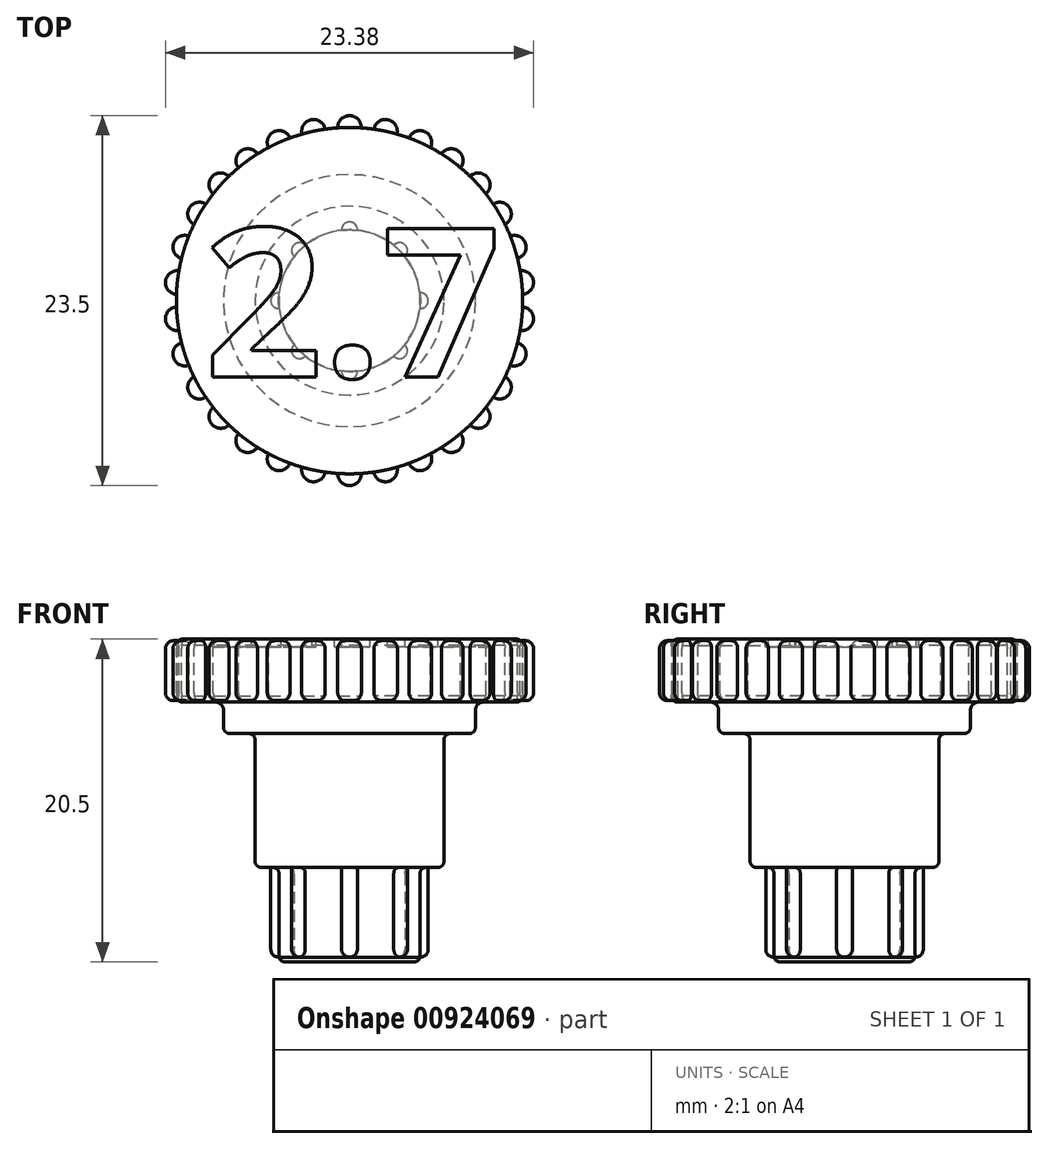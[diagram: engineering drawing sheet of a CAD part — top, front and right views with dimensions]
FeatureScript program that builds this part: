
annotation { "Feature Type Name" : "Feature", "Feature Type Description" : "" }
export const myFeature = defineFeature(function(context is Context, id is Id, definition is map)
    precondition{}
    {
        {
            var Q0;
            Q0=qCreatedBy(makeId("Front.planeOp"),FACE);
            var sketch = newSketch(context, id + "F0", { "sketchPlane" : qUnion([Q0])});
            skLineSegment(sketch, "E0", {"start": v(0, 0) * mm, "end": v(0, 20.5) * mm});
            skLineSegment(sketch, "E1", {"start": v(0, 20.5) * mm, "end": v(11, 20.5) * mm});
            skLineSegment(sketch, "E2", {"start": v(11, 20.5) * mm, "end": v(11, 16.5) * mm});
            skLineSegment(sketch, "E3", {"start": v(11, 16.5) * mm, "end": v(8, 16.5) * mm});
            skLineSegment(sketch, "E4", {"start": v(8, 16.5) * mm, "end": v(8, 14.5) * mm});
            skLineSegment(sketch, "E5", {"start": v(8, 14.5) * mm, "end": v(6, 14.5) * mm});
            skLineSegment(sketch, "E6", {"start": v(6, 14.5) * mm, "end": v(6, 6) * mm});
            skLineSegment(sketch, "E7", {"start": v(6, 6) * mm, "end": v(4.5, 6) * mm});
            skLineSegment(sketch, "E8", {"start": v(4.5, 6) * mm, "end": v(4.5, 0) * mm});
            skLineSegment(sketch, "E9", {"start": v(4.5, 0) * mm, "end": v(0, 0) * mm});
            skSolve(sketch);
        }
        {
            var Q0;
            Q0=makeQuery(id+"F0.imprint","IMPRINT",FACE,{"disambiguationData":[TD([[makeQuery(id+"F0.imprint","IMPRINT",EDGE,{"derivedFrom":sQuery(id+"F0.wireOp",EDGE,"E0")}),-1.0]])]});
            var Q1;
            Q1=sQuery(id+"F0.wireOp",EDGE,"E0");
            revolve(context, id + "F1", {"surfaceOperationType" : NewSurfaceOperationType.NEW, "entities" : qUnion([Q0]), "axis" : qUnion([Q1]), "revolveType" : RevolveType.FULL});
        }
        {
            var Q0;
            Q0=makeQuery(id+"F1.opRevolve","SWEPT_EDGE",EDGE,{"disambiguationData":[OSD([sQuery(id+"F0.wireOp",EDGE,"E3"),sQuery(id+"F0.wireOp",EDGE,"E4")])]});
            fillet(context, id + "F2", {"entities" : qUnion([Q0]), "radius" : 0.5 * mm, "tangentPropagation" : true, "allowEdgeOverflow" : false});
        }
        {
            var Q0;
            Q0=makeQuery(id+"F1.opRevolve","SWEPT_EDGE",EDGE,{"disambiguationData":[OSD([sQuery(id+"F0.wireOp",EDGE,"E2"),sQuery(id+"F0.wireOp",EDGE,"E3")])]});
            var Q1;
            Q1=makeQuery(id+"F1.opRevolve","SWEPT_EDGE",EDGE,{"disambiguationData":[OSD([sQuery(id+"F0.wireOp",EDGE,"E1"),sQuery(id+"F0.wireOp",EDGE,"E2")])]});
            fillet(context, id + "F3", {"entities" : qUnion([Q0, Q1]), "radius" : 0.4 * mm, "tangentPropagation" : true, "allowEdgeOverflow" : false});
        }
        {
            var Q0;
            Q0=makeQuery(id+"F1.opRevolve","SWEPT_FACE",FACE,{"disambiguationData":[OSD([sQuery(id+"F0.wireOp",EDGE,"E1")])]});
            cPlane(context, id + "F4", {"entities" : qUnion([Q0]), "cplaneType" : CPlaneType.OFFSET, "offset" : 0 * mm, "width" : 150 * mm, "height" : 150 * mm});
        }
        {
            var Q0;
            Q0=qCreatedBy(id+"F4.planeOp",FACE);
            var sketch = newSketch(context, id + "F5", { "sketchPlane" : qUnion([Q0])});
            skText(sketch, "E10", { "text": "2.7", "fontName": "OpenSans-Bold.ttf"});
            const initialGuessF5  = {"E10": [-0.00923, -0.00484, 1, 0, 0.0095]};
            skSetInitialGuess(sketch, initialGuessF5);
            skSolve(sketch);
        }
        {
            var Q0;
            Q0=qCreatedBy(id+"F4.planeOp",FACE);
            var sketch = newSketch(context, id + "F6", { "sketchPlane" : qUnion([Q0])});
            skCircle(sketch, "E11", {"center": v(0, 0) * mm, "radius": 11 * mm});
            skArc(sketch, "E12", {"start": v(-0.75, -10.97) * mm, "mid": v(0, -11.75) * mm, "end": v(0.75, -10.97) * mm});
            skSolve(sketch);
        }
        {
            var Q0;
            {var subQ0=sQuery(id+"F6.wireOp",EDGE,"E12");Q0=makeQuery(id+"F6.imprint","IMPRINT",FACE,{"disambiguationData":[TD([[makeQuery(id+"F6.imprint","IMPRINT",EDGE,{"derivedFrom":subQ0}),1.0]])]});}
            extrude(context, id + "F7", {"entities" : qUnion([Q0]), "operationType" : NewBodyOperationType.ADD, "oppositeDirection" : true, "depth" : 3.91 * mm, "offsetDistance" : 25 * mm, "hasSecondDirection" : true, "secondDirectionOppositeDirection" : true, "secondDirectionDepth" : 0.1 * mm});
        }
        {
            var Q0;
            Q0=makeQuery(id+"F7.opExtrude","CAP_EDGE",EDGE,{"disambiguationData":[OSD([sQuery(id+"F6.wireOp",EDGE,"E12")])],"isStart":true});
            var Q1;
            Q1=makeQuery(id+"F7.opExtrude","CAP_EDGE",EDGE,{"disambiguationData":[OSD([sQuery(id+"F6.wireOp",EDGE,"E12")])],"isStart":false});
            fillet(context, id + "F8", {"entities" : qUnion([Q0, Q1]), "radius" : 0.5 * mm, "tangentPropagation" : true, "allowEdgeOverflow" : false});
        }
        {
            var Q0;
            Q0=makeQuery(id+"F1.opRevolve","SWEPT_BODY",BODY,{"disambiguationData":[OSD([sQuery(id+"F0.wireOp",EDGE,"E0"),sQuery(id+"F0.wireOp",EDGE,"E1"),sQuery(id+"F0.wireOp",EDGE,"E2"),sQuery(id+"F0.wireOp",EDGE,"E3"),sQuery(id+"F0.wireOp",EDGE,"E4"),sQuery(id+"F0.wireOp",EDGE,"E5"),sQuery(id+"F0.wireOp",EDGE,"E6"),sQuery(id+"F0.wireOp",EDGE,"E7"),sQuery(id+"F0.wireOp",EDGE,"E8"),sQuery(id+"F0.wireOp",EDGE,"E9")])]});
            var Q1;
            Q1=makeQuery(id+"F1.opRevolve","SWEPT_FACE",FACE,{"disambiguationData":[OSD([sQuery(id+"F0.wireOp",EDGE,"E2")])]});
            circularPattern(context, id + "F9", {"operationType" : NewBodyOperationType.ADD, "entities" : qUnion([Q0]), "axis" : qUnion([Q1]), "angle" : 360 * degree, "instanceCount" : 30, "equalSpace" : true, "computeTransformsWithoutBuiltin" : true});
        }
        {
            var Q0;
            Q0=makeQuery(id+"F1.opRevolve","SWEPT_EDGE",EDGE,{"disambiguationData":[OSD([sQuery(id+"F0.wireOp",EDGE,"E6"),sQuery(id+"F0.wireOp",EDGE,"E7")])]});
            var Q1;
            Q1=makeQuery(id+"F1.opRevolve","SWEPT_EDGE",EDGE,{"disambiguationData":[OSD([sQuery(id+"F0.wireOp",EDGE,"E7"),sQuery(id+"F0.wireOp",EDGE,"E8")])]});
            var Q2;
            Q2=makeQuery(id+"F1.opRevolve","SWEPT_EDGE",EDGE,{"disambiguationData":[OSD([sQuery(id+"F0.wireOp",EDGE,"E5"),sQuery(id+"F0.wireOp",EDGE,"E6")])]});
            var Q3;
            Q3=makeQuery(id+"F1.opRevolve","SWEPT_EDGE",EDGE,{"disambiguationData":[OSD([sQuery(id+"F0.wireOp",EDGE,"E4"),sQuery(id+"F0.wireOp",EDGE,"E5")])]});
            var Q4;
            Q4=makeQuery(id+"F1.opRevolve","SWEPT_EDGE",EDGE,{"disambiguationData":[OSD([sQuery(id+"F0.wireOp",EDGE,"E8"),sQuery(id+"F0.wireOp",EDGE,"E9")])]});
            fillet(context, id + "F10", {"entities" : qUnion([Q0, Q1, Q2, Q3, Q4]), "radius" : 0.4 * mm, "tangentPropagation" : true, "allowEdgeOverflow" : false});
        }
        {
            var Q0;
            Q0=makeQuery(id+"F1.opRevolve","SWEPT_FACE",FACE,{"disambiguationData":[OSD([sQuery(id+"F0.wireOp",EDGE,"E9")])]});
            cPlane(context, id + "F11", {"entities" : qUnion([Q0]), "cplaneType" : CPlaneType.OFFSET, "offset" : 0.3 * mm, "oppositeDirection" : true, "width" : 150 * mm, "height" : 150 * mm});
        }
        {
            var Q0;
            Q0=qCreatedBy(id+"F11.planeOp",FACE);
            var sketch = newSketch(context, id + "F12", { "sketchPlane" : qUnion([Q0])});
            skArc(sketch, "E13", {"start": v(-0.5, 4.47) * mm, "mid": v(0, -4.5) * mm, "end": v(0.5, 4.47) * mm});
            skArc(sketch, "E14", {"start": v(0.5, 4.47) * mm, "mid": v(0, 5) * mm, "end": v(-0.5, 4.47) * mm});
            skArc(sketch, "E15.1.0", {"start": v(-2.8, 3.52) * mm, "mid": v(-3.54, 3.54) * mm, "end": v(-3.52, 2.8) * mm});
            skArc(sketch, "E15.2.0", {"start": v(-4.47, 0.5) * mm, "mid": v(-5, 0) * mm, "end": v(-4.47, -0.5) * mm});
            skArc(sketch, "E15.3.0", {"start": v(-3.52, -2.8) * mm, "mid": v(-3.54, -3.54) * mm, "end": v(-2.8, -3.52) * mm});
            skArc(sketch, "E15.4.0", {"start": v(-0.5, -4.47) * mm, "mid": v(0, -5) * mm, "end": v(0.5, -4.47) * mm});
            skArc(sketch, "E15.5.0", {"start": v(2.8, -3.52) * mm, "mid": v(3.54, -3.54) * mm, "end": v(3.52, -2.8) * mm});
            skArc(sketch, "E15.6.0", {"start": v(4.47, -0.5) * mm, "mid": v(5, 0) * mm, "end": v(4.47, 0.5) * mm});
            skArc(sketch, "E15.7.0", {"start": v(3.52, 2.8) * mm, "mid": v(3.54, 3.54) * mm, "end": v(2.8, 3.52) * mm});
            skSolve(sketch);
        }
        {
            var Q0;
            Q0=qSketchRegion(id+"F12",true);
            extrude(context, id + "F13", {"entities" : qUnion([Q0]), "operationType" : NewBodyOperationType.ADD, "oppositeDirection" : true, "depth" : 7 * mm, "offsetDistance" : 25 * mm});
        }
        {
            var Q0;
            Q0=makeQuery(id+"F13.opExtrude","CAP_EDGE",EDGE,{"disambiguationData":[OSD([sQuery(id+"F12.wireOp",EDGE,"E15.7.0")])],"isStart":true});
            var Q1;
            Q1=makeQuery(id+"F13.opExtrude","CAP_EDGE",EDGE,{"disambiguationData":[OSD([sQuery(id+"F12.wireOp",EDGE,"E15.6.0")])],"isStart":true});
            var Q2;
            Q2=makeQuery(id+"F13.opExtrude","CAP_EDGE",EDGE,{"disambiguationData":[OSD([sQuery(id+"F12.wireOp",EDGE,"E15.5.0")])],"isStart":true});
            var Q3;
            Q3=makeQuery(id+"F13.opExtrude","CAP_EDGE",EDGE,{"disambiguationData":[OSD([sQuery(id+"F12.wireOp",EDGE,"E14")])],"isStart":true});
            var Q4;
            Q4=makeQuery(id+"F13.opExtrude","CAP_EDGE",EDGE,{"disambiguationData":[OSD([sQuery(id+"F12.wireOp",EDGE,"E15.1.0")])],"isStart":true});
            var Q5;
            Q5=makeQuery(id+"F13.opExtrude","CAP_EDGE",EDGE,{"disambiguationData":[OSD([sQuery(id+"F12.wireOp",EDGE,"E15.4.0")])],"isStart":true});
            var Q6;
            Q6=makeQuery(id+"F13.opExtrude","CAP_EDGE",EDGE,{"disambiguationData":[OSD([sQuery(id+"F12.wireOp",EDGE,"E15.3.0")])],"isStart":true});
            var Q7;
            Q7=makeQuery(id+"F13.opExtrude","CAP_EDGE",EDGE,{"disambiguationData":[OSD([sQuery(id+"F12.wireOp",EDGE,"E15.2.0")])],"isStart":true});
            fillet(context, id + "F14", {"entities" : qUnion([Q0, Q1, Q2, Q3, Q4, Q5, Q6, Q7]), "radius" : 0.5 * mm, "tangentPropagation" : true, "allowEdgeOverflow" : false});
        }
        {
            var Q0;
            Q0=qSketchRegion(id+"F5",true);
            extrude(context, id + "F15", {"entities" : qUnion([Q0]), "operationType" : NewBodyOperationType.REMOVE, "oppositeDirection" : true, "depth" : 0.5 * mm, "offsetDistance" : 25 * mm});
        }
    });
